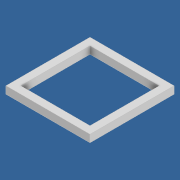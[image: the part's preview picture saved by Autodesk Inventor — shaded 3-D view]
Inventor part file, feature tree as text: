
AUTODESK INVENTOR PART (.ipt)
format: ipt  version: 2020 (Build 240168000, 168)  size: 80,896 bytes
history: native  units: in
note: dims shown in document units (in); Inventor stores cm internally (conversion verified against a paired STEP export)
features: extrude x1, sketch x1
ambient origin geometry x8: Origin, YZ Plane, XZ Plane, XY Plane, X Axis, Y Axis, Z Axis, Center Point
bodies: Solid1 (feature_tree)
feature tree (2):
  extrude  "Extrusion1"  Depth=0.6693in
  sketch  "Sketch1"  dims[d0=0.6693in d1=0.6693in d2=0.5512in d3=0.5512in d4=0.0591in d5=0.0in]
